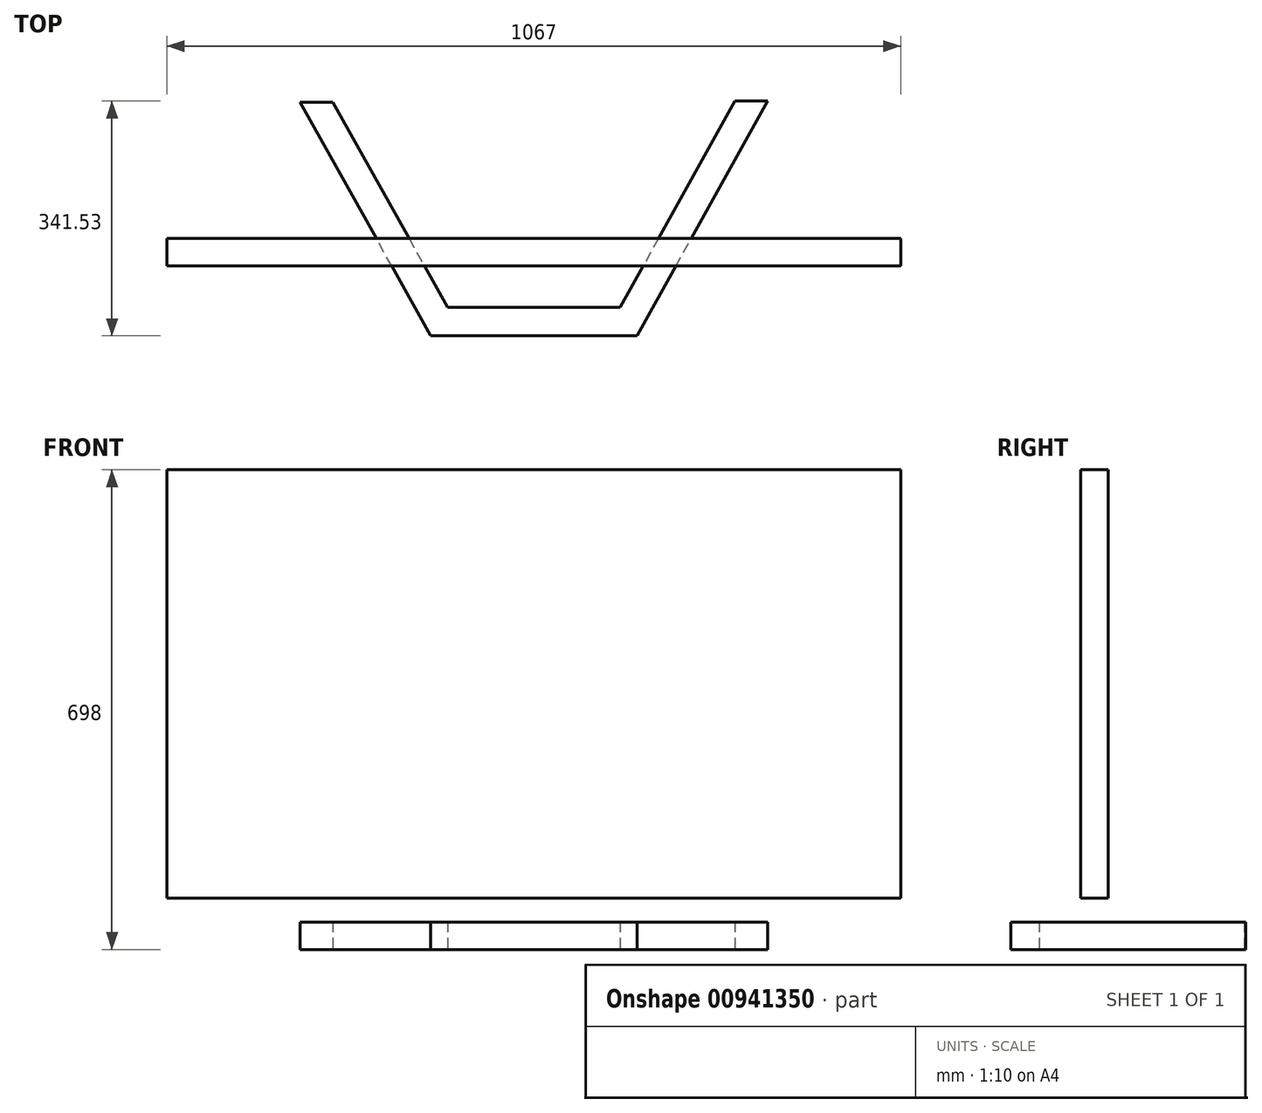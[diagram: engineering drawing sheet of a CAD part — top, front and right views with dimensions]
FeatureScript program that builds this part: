
annotation { "Feature Type Name" : "Feature", "Feature Type Description" : "" }
export const myFeature = defineFeature(function(context is Context, id is Id, definition is map)
    precondition{}
    {
        {
            var Q0;
            Q0=qCreatedBy(makeId("Front.planeOp"),FACE);
            var sketch = newSketch(context, id + "F0", { "sketchPlane" : qUnion([Q0])});
            skLineSegment(sketch, "E0.bottom", {"start": v(0, 0) * mm, "end": v(-1067, 0) * mm});
            skLineSegment(sketch, "E0.top", {"start": v(0, 623) * mm, "end": v(-1067, 623) * mm});
            skLineSegment(sketch, "E0.left", {"start": v(0, 0) * mm, "end": v(0, 623) * mm});
            skLineSegment(sketch, "E0.right", {"start": v(-1067, 0) * mm, "end": v(-1067, 623) * mm});
            skLineSegment(sketch, "E1", {"start": v(-533.5, 0) * mm, "end": v(-533.5, -75) * mm, "construction": true});
            skSolve(sketch);
        }
        {
            var Q0;
            Q0 = qSketchRegion(id + "F0", true);
            extrude(context, id + "F1", {"entities" : qUnion([Q0]), "depth" : 40 * mm, "offsetDistance" : 25 * mm});
        }
        {
            var Q0;
            Q0=qCreatedBy(makeId("Top.planeOp"),FACE);
            var sketch = newSketch(context, id + "F2", { "sketchPlane" : qUnion([Q0])});
            skLineSegment(sketch, "E2", {"start": v(-533.5, 0) * mm, "end": v(-533.5, -40) * mm, "construction": true});
            skLineSegment(sketch, "E3", {"start": v(-533.5, -40) * mm, "end": v(-383.5, -40) * mm, "construction": true});
            skLineSegment(sketch, "E4", {"start": v(-533.5, -40) * mm, "end": v(-683.5, -40) * mm, "construction": true});
            skSolve(sketch);
        }
        {
            var Q0;
            Q0=qCreatedBy(makeId("Top.planeOp"),FACE);
            cPlane(context, id + "F3", {"entities" : qUnion([Q0]), "cplaneType" : CPlaneType.OFFSET, "offset" : 75 * mm, "oppositeDirection" : true, "width" : 150 * mm, "height" : 150 * mm});
        }
        {
            var Q0;
            Q0=qCreatedBy(id+"F3.planeOp",FACE);
            var sketch = newSketch(context, id + "F4", { "sketchPlane" : qUnion([Q0])});
            skLineSegment(sketch, "E5.MirrorCS", {"start": v(-683.5, -141.53) * mm, "end": v(-873.5, 198.47) * mm});
            skLineSegment(sketch, "E6.MirrorCS", {"start": v(-193.5, 200) * mm, "end": v(-241.08, 200) * mm});
            skLineSegment(sketch, "E7.MirrorCS", {"start": v(-825.92, 198.47) * mm, "end": v(-659.13, -100) * mm});
            skLineSegment(sketch, "E8.MirrorCS", {"start": v(-407.87, -100) * mm, "end": v(-659.13, -100) * mm});
            skLineSegment(sketch, "E9.MirrorCS", {"start": v(-533.5, -100) * mm, "end": v(-533.5, -141.53) * mm, "construction": true});
            skLineSegment(sketch, "E10.MirrorCS", {"start": v(-407.87, -100) * mm, "end": v(-371.61, -120.26) * mm, "construction": true});
            skLineSegment(sketch, "E11.MirrorCS", {"start": v(-383.5, -141.53) * mm, "end": v(-193.5, 200) * mm});
            skLineSegment(sketch, "E12.MirrorCS", {"start": v(-241.08, 200) * mm, "end": v(-407.87, -100) * mm});
            skLineSegment(sketch, "E13.MirrorCS", {"start": v(-683.5, -141.53) * mm, "end": v(-383.5, -141.53) * mm});
            skLineSegment(sketch, "E14.MirrorCS", {"start": v(-825.92, 198.47) * mm, "end": v(-873.5, 198.47) * mm});
            skSolve(sketch);
        }
        {
            var Q0;
            Q0=makeQuery(id+"F4.imprint","IMPRINT",FACE,{"disambiguationData":[TD([[makeQuery(id+"F4.imprint","IMPRINT",EDGE,{"derivedFrom":sQuery(id+"F4.wireOp",EDGE,"E5.MirrorCS")}),-1.0]])]});
            extrude(context, id + "F5", {"entities" : qUnion([Q0]), "depth" : 40 * mm, "offsetDistance" : 25 * mm});
        }
    });
